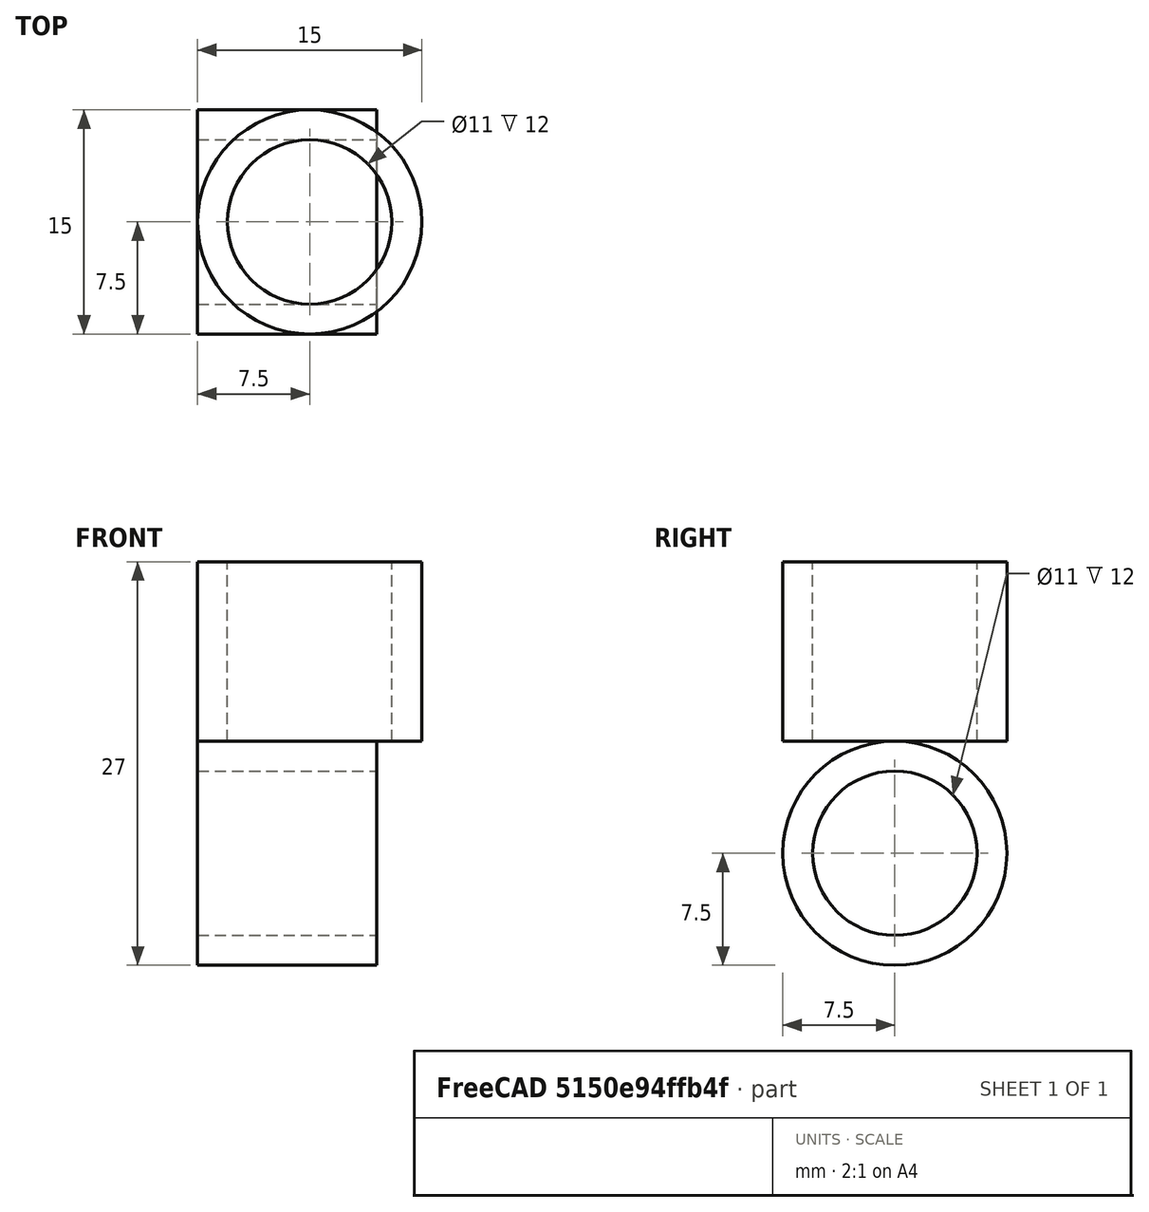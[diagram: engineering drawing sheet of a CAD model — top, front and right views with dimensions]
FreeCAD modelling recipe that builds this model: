
FCSTD DOCUMENT  (FreeCAD 0.15R4664 (Git))
Label: x_linear_bearing_spacer
License: All rights reserved
LicenseURL: http://en.wikipedia.org/wiki/All_rights_reserved
objects: Part::Feature×2, Part::Cylinder×2, Mesh::Feature×1, Part::Cut×1
note: 5 computed .brp shape members not serialized (recipe doc carries the construction recipe); baked Part::Feature solids carry a one-line shape summary decoded from their .brp

FEATURE [Mesh::Feature] Xlinearbearingsspacer
FEATURE [Part::Feature] Xlinearbearingsspacer001001  label="Xlinearbearingsspacer002"
  shape: bbox 15 x 15 x 21 mm, 799 faces, 0 solids (baked)
FEATURE [Part::Cylinder] Cylinder  label="Cilindro"
  Angle = 360
  Height = 14
  Placement = pos=(7.5,7.5,-1) rot=(0,0,1;0rad)
  Radius = 5.5
FEATURE [Part::Cylinder] Cylinder001  label="Cilindro001"
  Angle = 360
  Height = 12
  Placement = pos=(7.5,7.5,0) rot=(0,0,1;0rad)
  Radius = 7.5
FEATURE [Part::Cut] Cut  label="x_linear_bearing_spacer"
  Base = -> Cylinder001
  Tool = -> Cylinder
FEATURE [Part::Feature] Cut_solid  label="x_linear_bearing_spacer (Solid)"
  Placement = pos=(0,0,0) rot=(0,1,0;1.5708rad)
  shape: bbox 12 x 15 x 15 mm, 4 faces (baked)
